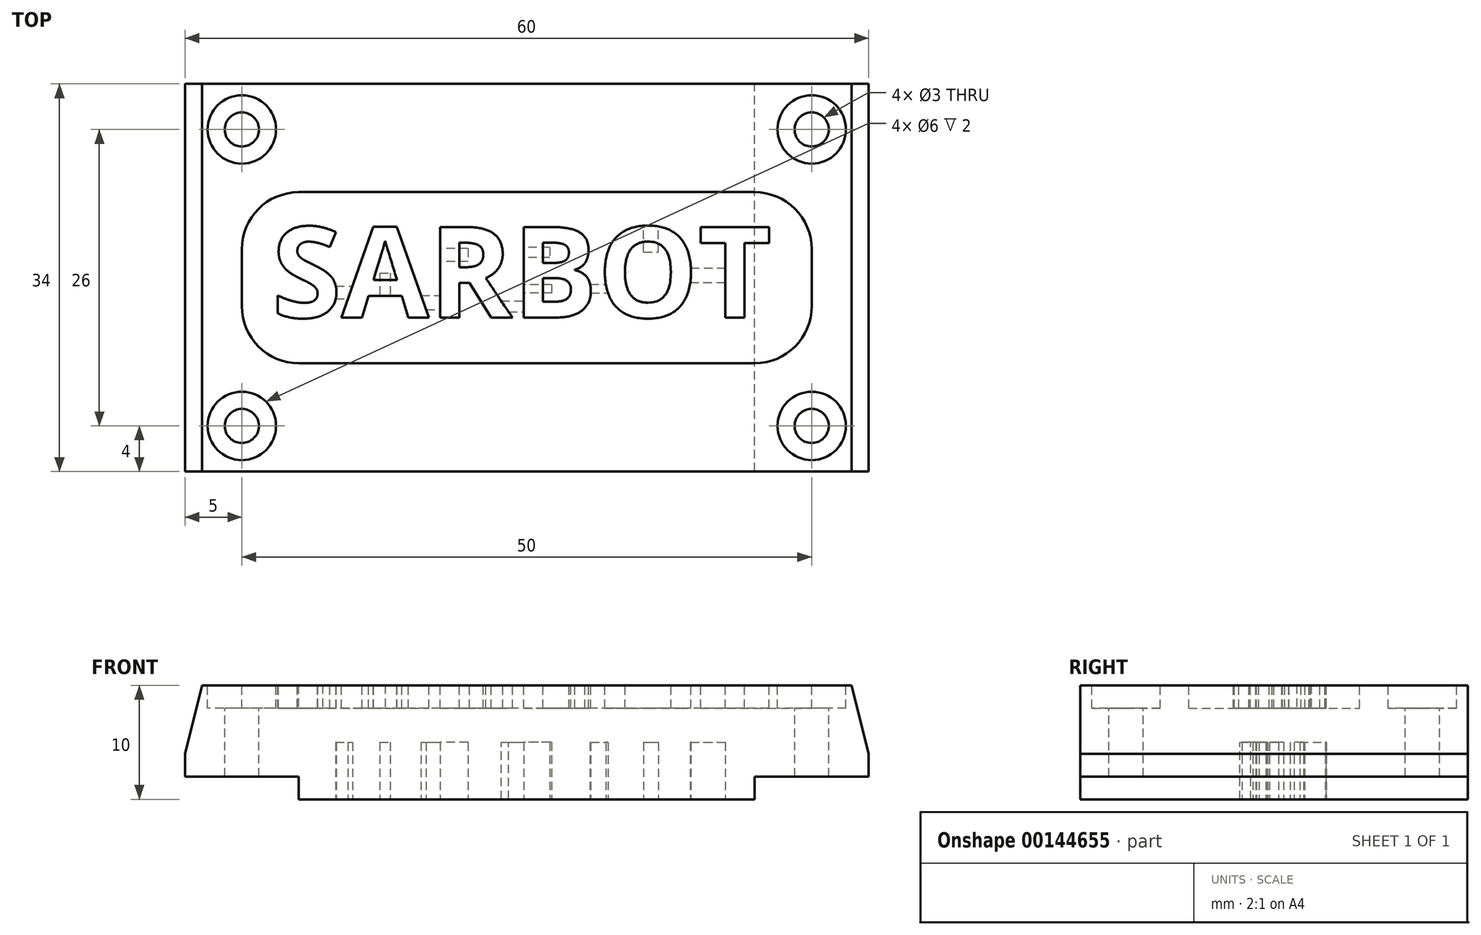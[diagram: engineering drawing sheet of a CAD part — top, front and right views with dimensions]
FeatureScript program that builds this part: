
annotation { "Feature Type Name" : "Feature", "Feature Type Description" : "" }
export const myFeature = defineFeature(function(context is Context, id is Id, definition is map)
    precondition{}
    {
        {
            var Q0;
            Q0=qCreatedBy(makeId("Top.planeOp"),FACE);
            var sketch = newSketch(context, id + "F0", { "sketchPlane" : qUnion([Q0])});
            skLineSegment(sketch, "E0.bottom", {"start": v(30, -17) * mm, "end": v(-30, -17) * mm});
            skLineSegment(sketch, "E0.top", {"start": v(30, 17) * mm, "end": v(-30, 17) * mm});
            skLineSegment(sketch, "E0.left", {"start": v(30, -17) * mm, "end": v(30, 17) * mm});
            skLineSegment(sketch, "E0.right", {"start": v(-30, -17) * mm, "end": v(-30, 17) * mm});
            skPoint(sketch, "E0.middle", {"position": v(0, 0) * mm});
            skSolve(sketch);
        }
        {
            var Q0;
            Q0=makeQuery(id+"F0.imprint","IMPRINT",FACE,{"disambiguationData":[TD([[makeQuery(id+"F0.imprint","IMPRINT",EDGE,{"derivedFrom":sQuery(id+"F0.wireOp",EDGE,"E0.bottom")}),-1.0]])]});
            extrude(context, id + "F1", {"entities" : qUnion([Q0]), "depth" : 10 * mm});
        }
        {
            var Q0;
            Q0=makeQuery(id+"F1.opExtrude","CAP_EDGE",EDGE,{"disambiguationData":[OSD([sQuery(id+"F0.wireOp",EDGE,"E0.right")])],"isStart":false});
            var Q1;
            Q1=makeQuery(id+"F1.opExtrude","CAP_EDGE",EDGE,{"disambiguationData":[OSD([sQuery(id+"F0.wireOp",EDGE,"E0.left")])],"isStart":false});
            chamfer(context, id + "F2", {"entities" : qUnion([Q0, Q1]), "chamferType" : ChamferType.TWO_OFFSETS, "width1" : 6 * mm, "oppositeDirection" : false, "width2" : 1.5 * mm, "tangentPropagation" : true});
        }
        {
            var Q0;
            Q0=makeQuery(id+"F1.opExtrude","CAP_FACE",FACE,{"disambiguationData":[OSD([sQuery(id+"F0.wireOp",EDGE,"E0.bottom"),sQuery(id+"F0.wireOp",EDGE,"E0.top"),sQuery(id+"F0.wireOp",EDGE,"E0.left"),sQuery(id+"F0.wireOp",EDGE,"E0.right")])],"isStart":true});
            var sketch = newSketch(context, id + "F3", { "sketchPlane" : qUnion([Q0])});
            skLineSegment(sketch, "E1.bottom", {"start": v(20, 17) * mm, "end": v(-20, 17) * mm});
            skLineSegment(sketch, "E1.top", {"start": v(20, -17) * mm, "end": v(-20, -17) * mm});
            skLineSegment(sketch, "E1.left", {"start": v(20, 17) * mm, "end": v(20, -17) * mm});
            skLineSegment(sketch, "E1.right", {"start": v(-20, 17) * mm, "end": v(-20, -17) * mm});
            skPoint(sketch, "E1.middle", {"position": v(0, 0) * mm});
            skSolve(sketch);
        }
        {
            var Q0;
            {var subQ0=sQuery(id+"F3.wireOp",EDGE,"E1.right");Q0=makeQuery(id+"F3.imprint","IMPRINT",FACE,{"disambiguationData":[TD([[makeQuery(id+"F3.imprint","IMPRINT",EDGE,{"derivedFrom":subQ0}),-1.0]])]});}
            var Q1;
            {var subQ0=sQuery(id+"F3.wireOp",EDGE,"E1.left");Q1=makeQuery(id+"F3.imprint","IMPRINT",FACE,{"disambiguationData":[TD([[makeQuery(id+"F3.imprint","IMPRINT",EDGE,{"derivedFrom":subQ0}),1.0]])]});}
            extrude(context, id + "F4", {"entities" : qUnion([Q0, Q1]), "operationType" : NewBodyOperationType.REMOVE, "oppositeDirection" : true, "depth" : 2 * mm});
        }
        {
            var Q0;
            Q0=makeQuery(id+"F1.opExtrude","CAP_FACE",FACE,{"disambiguationData":[OSD([sQuery(id+"F0.wireOp",EDGE,"E0.bottom"),sQuery(id+"F0.wireOp",EDGE,"E0.top"),sQuery(id+"F0.wireOp",EDGE,"E0.left"),sQuery(id+"F0.wireOp",EDGE,"E0.right")])],"isStart":false});
            var sketch = newSketch(context, id + "F5", { "sketchPlane" : qUnion([Q0])});
            skLineSegment(sketch, "E2.bottom", {"start": v(25, 13) * mm, "end": v(-25, 13) * mm});
            skLineSegment(sketch, "E2.top", {"start": v(25, -13) * mm, "end": v(-25, -13) * mm});
            skLineSegment(sketch, "E2.left", {"start": v(25, 13) * mm, "end": v(25, -13) * mm});
            skLineSegment(sketch, "E2.right", {"start": v(-25, 13) * mm, "end": v(-25, -13) * mm});
            skPoint(sketch, "E2.middle", {"position": v(0, 0) * mm});
            skText(sketch, "E3", { "text": "SARBOT", "fontName": "OpenSans-Bold.ttf"});
            skLineSegment(sketch, "E4.bottom", {"start": v(25, 7.5) * mm, "end": v(-25, 7.5) * mm});
            skLineSegment(sketch, "E4.top", {"start": v(25, -7.5) * mm, "end": v(-25, -7.5) * mm});
            skLineSegment(sketch, "E4.left", {"start": v(25, 7.5) * mm, "end": v(25, -7.5) * mm});
            skLineSegment(sketch, "E4.right", {"start": v(-25, 7.5) * mm, "end": v(-25, -7.5) * mm});
            const initialGuessF5  = {"E3": [-0.02238, -0.00349, 1, 0, 0.008]};
            skSetInitialGuess(sketch, initialGuessF5);
            skSolve(sketch);
        }
        {
            var Q0;
            Q0=sQuery(id+"F5.wireOp",VERTEX,"E2.right.start");
            var Q1;
            Q1=sQuery(id+"F5.wireOp",VERTEX,"E2.bottom.start");
            var Q2;
            Q2=sQuery(id+"F5.wireOp",VERTEX,"E2.left.end");
            var Q3;
            Q3=sQuery(id+"F5.wireOp",VERTEX,"E2.right.end");
            var Q4;
            Q4=makeQuery(id+"F1.opExtrude","SWEPT_BODY",BODY,{"disambiguationData":[OSD([sQuery(id+"F0.wireOp",EDGE,"E0.bottom"),sQuery(id+"F0.wireOp",EDGE,"E0.top"),sQuery(id+"F0.wireOp",EDGE,"E0.left"),sQuery(id+"F0.wireOp",EDGE,"E0.right")])]});
            hole(context, id + "F6", {"style" : HoleStyle.C_BORE, "endStyle" : HoleEndStyle.THROUGH, "holeDiameter" : 3 * mm, "cBoreDiameter" : 6 * mm, "cBoreDepth" : 2 * mm, "startFromSketch" : true, "locations" : qUnion([Q0, Q1, Q2, Q3]), "scope" : qUnion([Q4]), "isTappedThrough" : true});
        }
        {
            var Q0;
            Q0=makeQuery(id+"F5.imprint","IMPRINT",FACE,{"disambiguationData":[TD([[makeQuery(id+"F5.imprint","IMPRINT",EDGE,{"derivedFrom":sQuery(id+"F5.wireOp",EDGE,"E3.sketch_text.stroke-0")}),-1.0]])]});
            var Q1;
            Q1=makeQuery(id+"F5.imprint","IMPRINT",FACE,{"disambiguationData":[TD([[makeQuery(id+"F5.imprint","IMPRINT",EDGE,{"derivedFrom":sQuery(id+"F5.wireOp",EDGE,"E3.sketch_text.stroke-28")}),-1.0]])]});
            var Q2;
            Q2=makeQuery(id+"F5.imprint","IMPRINT",FACE,{"disambiguationData":[TD([[makeQuery(id+"F5.imprint","IMPRINT",EDGE,{"derivedFrom":sQuery(id+"F5.wireOp",EDGE,"E3.sketch_text.stroke-40")}),-1.0]])]});
            var Q3;
            Q3=makeQuery(id+"F5.imprint","IMPRINT",FACE,{"disambiguationData":[TD([[makeQuery(id+"F5.imprint","IMPRINT",EDGE,{"derivedFrom":sQuery(id+"F5.wireOp",EDGE,"E3.sketch_text.stroke-59")}),-1.0]])]});
            var Q4;
            Q4=makeQuery(id+"F5.imprint","IMPRINT",FACE,{"disambiguationData":[TD([[makeQuery(id+"F5.imprint","IMPRINT",EDGE,{"derivedFrom":sQuery(id+"F5.wireOp",EDGE,"E3.sketch_text.stroke-84")}),-1.0]])]});
            var Q5;
            Q5=makeQuery(id+"F5.imprint","IMPRINT",FACE,{"disambiguationData":[TD([[makeQuery(id+"F5.imprint","IMPRINT",EDGE,{"derivedFrom":sQuery(id+"F5.wireOp",EDGE,"E3.sketch_text.stroke-98")}),-1.0]])]});
            extrude(context, id + "F7", {"entities" : qUnion([Q0, Q1, Q2, Q3, Q4, Q5]), "operationType" : NewBodyOperationType.REMOVE, "oppositeDirection" : true, "depth" : 25 * mm});
        }
        {
            var Q0;
            Q0=makeQuery(id+"F5.imprint","IMPRINT",FACE,{"disambiguationData":[TD([[makeQuery(id+"F5.imprint","IMPRINT",EDGE,{"derivedFrom":sQuery(id+"F5.wireOp",EDGE,"E3.sketch_text.stroke-0")}),-1.0]])]});
            var Q1;
            Q1=makeQuery(id+"F5.imprint","IMPRINT",FACE,{"disambiguationData":[TD([[makeQuery(id+"F5.imprint","IMPRINT",EDGE,{"derivedFrom":sQuery(id+"F5.wireOp",EDGE,"E3.sketch_text.stroke-28")}),-1.0]])]});
            var Q2;
            Q2=makeQuery(id+"F5.imprint","IMPRINT",FACE,{"disambiguationData":[TD([[makeQuery(id+"F5.imprint","IMPRINT",EDGE,{"derivedFrom":sQuery(id+"F5.wireOp",EDGE,"E3.sketch_text.stroke-40")}),-1.0]])]});
            var Q3;
            Q3=makeQuery(id+"F5.imprint","IMPRINT",FACE,{"disambiguationData":[TD([[makeQuery(id+"F5.imprint","IMPRINT",EDGE,{"derivedFrom":sQuery(id+"F5.wireOp",EDGE,"E3.sketch_text.stroke-59")}),-1.0]])]});
            var Q4;
            Q4=makeQuery(id+"F5.imprint","IMPRINT",FACE,{"disambiguationData":[TD([[makeQuery(id+"F5.imprint","IMPRINT",EDGE,{"derivedFrom":sQuery(id+"F5.wireOp",EDGE,"E3.sketch_text.stroke-84")}),-1.0]])]});
            var Q5;
            Q5=makeQuery(id+"F5.imprint","IMPRINT",FACE,{"disambiguationData":[TD([[makeQuery(id+"F5.imprint","IMPRINT",EDGE,{"derivedFrom":sQuery(id+"F5.wireOp",EDGE,"E3.sketch_text.stroke-98")}),-1.0]])]});
            extrude(context, id + "F8", {"entities" : qUnion([Q0, Q1, Q2, Q3, Q4, Q5]), "oppositeDirection" : true, "depth" : 10 * mm});
        }
        {
            var Q0;
            Q0=makeQuery(id+"F5.imprint","IMPRINT",FACE,{"disambiguationData":[TD([[makeQuery(id+"F5.imprint","IMPRINT",EDGE,{"derivedFrom":sQuery(id+"F5.wireOp",EDGE,"E3.sketch_text.stroke-0")}),1.0]])]});
            var Q1;
            Q1=makeQuery(id+"F5.imprint","IMPRINT",FACE,{"disambiguationData":[TD([[makeQuery(id+"F5.imprint","IMPRINT",EDGE,{"derivedFrom":sQuery(id+"F5.wireOp",EDGE,"E3.sketch_text.stroke-36")}),1.0]])]});
            var Q2;
            Q2=makeQuery(id+"F5.imprint","IMPRINT",FACE,{"disambiguationData":[TD([[makeQuery(id+"F5.imprint","IMPRINT",EDGE,{"derivedFrom":sQuery(id+"F5.wireOp",EDGE,"E3.sketch_text.stroke-40")}),1.0]])]});
            var Q3;
            Q3=makeQuery(id+"F5.imprint","IMPRINT",FACE,{"disambiguationData":[TD([[makeQuery(id+"F5.imprint","IMPRINT",EDGE,{"derivedFrom":sQuery(id+"F5.wireOp",EDGE,"E3.sketch_text.stroke-71")}),1.0]])]});
            var Q4;
            Q4=makeQuery(id+"F5.imprint","IMPRINT",FACE,{"disambiguationData":[TD([[makeQuery(id+"F5.imprint","IMPRINT",EDGE,{"derivedFrom":sQuery(id+"F5.wireOp",EDGE,"E3.sketch_text.stroke-78")}),1.0]])]});
            var Q5;
            Q5=makeQuery(id+"F5.imprint","IMPRINT",FACE,{"disambiguationData":[TD([[makeQuery(id+"F5.imprint","IMPRINT",EDGE,{"derivedFrom":sQuery(id+"F5.wireOp",EDGE,"E3.sketch_text.stroke-92")}),1.0]])]});
            extrude(context, id + "F9", {"entities" : qUnion([Q0, Q1, Q2, Q3, Q4, Q5]), "operationType" : NewBodyOperationType.REMOVE, "oppositeDirection" : true, "depth" : 2 * mm});
        }
        {
            var Q0;
            Q0=makeQuery(id+"F9.boolean.opBoolean","COPY",EDGE,{"derivedFrom":makeQuery(id+"F9.opExtrude","SWEPT_EDGE",EDGE,{"disambiguationData":[OSD([sQuery(id+"F5.wireOp",EDGE,"E2.right"),sQuery(id+"F5.wireOp",EDGE,"E4.bottom"),sQuery(id+"F5.wireOp",EDGE,"E4.right")])]})});
            var Q1;
            Q1=makeQuery(id+"F9.boolean.opBoolean","COPY",EDGE,{"derivedFrom":makeQuery(id+"F9.opExtrude","SWEPT_EDGE",EDGE,{"disambiguationData":[OSD([sQuery(id+"F5.wireOp",EDGE,"E2.left"),sQuery(id+"F5.wireOp",EDGE,"E4.bottom"),sQuery(id+"F5.wireOp",EDGE,"E4.left")])]})});
            var Q2;
            Q2=makeQuery(id+"F9.boolean.opBoolean","COPY",EDGE,{"derivedFrom":makeQuery(id+"F9.opExtrude","SWEPT_EDGE",EDGE,{"disambiguationData":[OSD([sQuery(id+"F5.wireOp",EDGE,"E2.right"),sQuery(id+"F5.wireOp",EDGE,"E4.top"),sQuery(id+"F5.wireOp",EDGE,"E4.right")])]})});
            var Q3;
            Q3=makeQuery(id+"F9.boolean.opBoolean","COPY",EDGE,{"derivedFrom":makeQuery(id+"F9.opExtrude","SWEPT_EDGE",EDGE,{"disambiguationData":[OSD([sQuery(id+"F5.wireOp",EDGE,"E2.left"),sQuery(id+"F5.wireOp",EDGE,"E4.top"),sQuery(id+"F5.wireOp",EDGE,"E4.left")])]})});
            fillet(context, id + "F10", {"entities" : qUnion([Q0, Q1, Q2, Q3]), "radius" : 5 * mm, "tangentPropagation" : true, "allowEdgeOverflow" : false});
        }
        {
            var Q0;
            {var subQ0=sQuery(id+"F0.wireOp",EDGE,"E0.bottom");var subQ1=sQuery(id+"F0.wireOp",EDGE,"E0.top");Q0=makeQuery(id+"F7.boolean.opBoolean","SPLIT",FACE,{"disambiguationData":[TD([makeQuery(id+"F1.opExtrude","SWEPT_FACE",FACE,{"disambiguationData":[OSD([subQ0])]})])],"derivedFrom":makeQuery(id+"F1.opExtrude","CAP_FACE",FACE,{"disambiguationData":[OSD([subQ0,subQ1,sQuery(id+"F0.wireOp",EDGE,"E0.left"),sQuery(id+"F0.wireOp",EDGE,"E0.right")])],"isStart":true})});}
            var sketch = newSketch(context, id + "F11", { "sketchPlane" : qUnion([Q0])});
            skLineSegment(sketch, "E5.bottom", {"start": v(-12.9, -0.4) * mm, "end": v(-11.99, -0.4) * mm});
            skLineSegment(sketch, "E5.top", {"start": v(-12.9, 2.92) * mm, "end": v(-11.99, 2.92) * mm});
            skLineSegment(sketch, "E5.left", {"start": v(-12.9, -0.4) * mm, "end": v(-12.9, 2.92) * mm});
            skLineSegment(sketch, "E5.right", {"start": v(-11.99, -0.4) * mm, "end": v(-11.99, 2.92) * mm});
            skLineSegment(sketch, "E6.bottom", {"start": v(-5.16, -2.56) * mm, "end": v(-8.52, -2.56) * mm});
            skLineSegment(sketch, "E6.top", {"start": v(-5.16, -1.41) * mm, "end": v(-8.52, -1.41) * mm});
            skLineSegment(sketch, "E6.left", {"start": v(-5.16, -2.56) * mm, "end": v(-5.16, -1.41) * mm});
            skLineSegment(sketch, "E6.right", {"start": v(-8.52, -2.56) * mm, "end": v(-8.52, -1.41) * mm});
            skLineSegment(sketch, "E7.bottom", {"start": v(2.03, -2.67) * mm, "end": v(-1.26, -2.67) * mm});
            skLineSegment(sketch, "E7.top", {"start": v(2.03, -1.76) * mm, "end": v(-1.26, -1.76) * mm});
            skLineSegment(sketch, "E7.left", {"start": v(2.03, -2.67) * mm, "end": v(2.03, -1.76) * mm});
            skLineSegment(sketch, "E7.right", {"start": v(-1.26, -2.67) * mm, "end": v(-1.26, -1.76) * mm});
            skLineSegment(sketch, "E8.bottom", {"start": v(2.18, 0.6) * mm, "end": v(-1.22, 0.6) * mm});
            skLineSegment(sketch, "E8.top", {"start": v(2.18, 1.34) * mm, "end": v(-1.22, 1.34) * mm});
            skLineSegment(sketch, "E8.left", {"start": v(2.18, 0.6) * mm, "end": v(2.18, 1.34) * mm});
            skLineSegment(sketch, "E8.right", {"start": v(-1.22, 0.6) * mm, "end": v(-1.22, 1.34) * mm});
            skLineSegment(sketch, "E9.bottom", {"start": v(10.24, -2.24) * mm, "end": v(11.56, -2.24) * mm});
            skLineSegment(sketch, "E9.top", {"start": v(10.24, -5.78) * mm, "end": v(11.56, -5.78) * mm});
            skLineSegment(sketch, "E9.left", {"start": v(10.24, -2.24) * mm, "end": v(10.24, -5.78) * mm});
            skLineSegment(sketch, "E9.right", {"start": v(11.56, -2.24) * mm, "end": v(11.56, -5.78) * mm});
            skLineSegment(sketch, "E10.bottom", {"start": v(-17.47, 1.86) * mm, "end": v(-14.77, 1.86) * mm});
            skLineSegment(sketch, "E10.top", {"start": v(-17.47, 0.73) * mm, "end": v(-14.77, 0.73) * mm});
            skLineSegment(sketch, "E10.left", {"start": v(-17.47, 1.86) * mm, "end": v(-17.47, 0.73) * mm});
            skLineSegment(sketch, "E10.right", {"start": v(-14.77, 1.86) * mm, "end": v(-14.77, 0.73) * mm});
            skLineSegment(sketch, "E11.bottom", {"start": v(-9.8, 2.81) * mm, "end": v(-6.93, 2.81) * mm});
            skLineSegment(sketch, "E11.top", {"start": v(-9.8, 1.56) * mm, "end": v(-6.93, 1.56) * mm});
            skLineSegment(sketch, "E11.left", {"start": v(-9.8, 2.81) * mm, "end": v(-9.8, 1.56) * mm});
            skLineSegment(sketch, "E11.right", {"start": v(-6.93, 2.81) * mm, "end": v(-6.93, 1.56) * mm});
            skLineSegment(sketch, "E12.bottom", {"start": v(-2.64, 3) * mm, "end": v(0.52, 3) * mm});
            skLineSegment(sketch, "E12.top", {"start": v(-2.64, 2.05) * mm, "end": v(0.52, 2.05) * mm});
            skLineSegment(sketch, "E12.left", {"start": v(-2.64, 3) * mm, "end": v(-2.64, 2.05) * mm});
            skLineSegment(sketch, "E12.right", {"start": v(0.52, 3) * mm, "end": v(0.52, 2.05) * mm});
            skLineSegment(sketch, "E13.bottom", {"start": v(4.78, 1.34) * mm, "end": v(7.72, 1.34) * mm});
            skLineSegment(sketch, "E13.top", {"start": v(4.78, 0.58) * mm, "end": v(7.72, 0.58) * mm});
            skLineSegment(sketch, "E13.left", {"start": v(4.78, 1.34) * mm, "end": v(4.78, 0.58) * mm});
            skLineSegment(sketch, "E13.right", {"start": v(7.72, 1.34) * mm, "end": v(7.72, 0.58) * mm});
            skLineSegment(sketch, "E14.bottom", {"start": v(13.43, 0.42) * mm, "end": v(18.24, 0.42) * mm});
            skLineSegment(sketch, "E14.top", {"start": v(13.43, -0.84) * mm, "end": v(18.24, -0.84) * mm});
            skLineSegment(sketch, "E14.left", {"start": v(13.43, 0.42) * mm, "end": v(13.43, -0.84) * mm});
            skLineSegment(sketch, "E14.right", {"start": v(18.24, 0.42) * mm, "end": v(18.24, -0.84) * mm});
            skSolve(sketch);
        }
        {
            var Q0;
            {var subQ0=sQuery(id+"F11.wireOp",EDGE,"E5.top");Q0=makeQuery(id+"F11.imprint","IMPRINT",FACE,{"disambiguationData":[TD([[makeQuery(id+"F11.imprint","IMPRINT",EDGE,{"derivedFrom":subQ0}),-1.0]])]});}
            var Q1;
            {var subQ0=sQuery(id+"F11.wireOp",EDGE,"E5.bottom");Q1=makeQuery(id+"F11.imprint","IMPRINT",FACE,{"disambiguationData":[TD([[makeQuery(id+"F11.imprint","IMPRINT",EDGE,{"derivedFrom":subQ0}),1.0]])]});}
            var Q2;
            {var subQ0=sQuery(id+"F11.wireOp",EDGE,"E6.right");Q2=makeQuery(id+"F11.imprint","IMPRINT",FACE,{"disambiguationData":[TD([[makeQuery(id+"F11.imprint","IMPRINT",EDGE,{"derivedFrom":subQ0}),-1.0]])]});}
            var Q3;
            {var subQ0=sQuery(id+"F11.wireOp",EDGE,"E6.left");Q3=makeQuery(id+"F11.imprint","IMPRINT",FACE,{"disambiguationData":[TD([[makeQuery(id+"F11.imprint","IMPRINT",EDGE,{"derivedFrom":subQ0}),1.0]])]});}
            var Q4;
            {var subQ0=sQuery(id+"F11.wireOp",EDGE,"E7.left");Q4=makeQuery(id+"F11.imprint","IMPRINT",FACE,{"disambiguationData":[TD([[makeQuery(id+"F11.imprint","IMPRINT",EDGE,{"derivedFrom":subQ0}),1.0]])]});}
            var Q5;
            {var subQ0=sQuery(id+"F11.wireOp",EDGE,"E7.right");Q5=makeQuery(id+"F11.imprint","IMPRINT",FACE,{"disambiguationData":[TD([[makeQuery(id+"F11.imprint","IMPRINT",EDGE,{"derivedFrom":subQ0}),-1.0]])]});}
            var Q6;
            {var subQ0=sQuery(id+"F11.wireOp",EDGE,"E8.right");Q6=makeQuery(id+"F11.imprint","IMPRINT",FACE,{"disambiguationData":[TD([[makeQuery(id+"F11.imprint","IMPRINT",EDGE,{"derivedFrom":subQ0}),-1.0]])]});}
            var Q7;
            {var subQ0=sQuery(id+"F11.wireOp",EDGE,"E8.left");Q7=makeQuery(id+"F11.imprint","IMPRINT",FACE,{"disambiguationData":[TD([[makeQuery(id+"F11.imprint","IMPRINT",EDGE,{"derivedFrom":subQ0}),1.0]])]});}
            var Q8;
            {var subQ7=sQuery(id+"F11.wireOp",EDGE,"E9.top");Q8=makeQuery(id+"F11.imprint","IMPRINT",FACE,{"disambiguationData":[TD([[makeQuery(id+"F11.imprint","IMPRINT",EDGE,{"derivedFrom":subQ7}),1.0]])]});}
            var Q9;
            {var subQ8=sQuery(id+"F11.wireOp",EDGE,"E9.bottom");Q9=makeQuery(id+"F11.imprint","IMPRINT",FACE,{"disambiguationData":[TD([[makeQuery(id+"F11.imprint","IMPRINT",EDGE,{"derivedFrom":subQ8}),-1.0]])]});}
            extrude(context, id + "F12", {"entities" : qUnion([Q0, Q1, Q2, Q3, Q4, Q5, Q6, Q7, Q8, Q9]), "operationType" : NewBodyOperationType.ADD, "oppositeDirection" : true, "depth" : 5 * mm});
        }
        {
            var Q0;
            {var subQ0=sQuery(id+"F11.wireOp",EDGE,"E5.bottom");Q0=makeQuery(id+"F11.imprint","IMPRINT",FACE,{"disambiguationData":[TD([[makeQuery(id+"F11.imprint","IMPRINT",EDGE,{"derivedFrom":subQ0}),1.0]])]});}
            var Q1;
            {var subQ0=sQuery(id+"F11.wireOp",EDGE,"E6.left");Q1=makeQuery(id+"F11.imprint","IMPRINT",FACE,{"disambiguationData":[TD([[makeQuery(id+"F11.imprint","IMPRINT",EDGE,{"derivedFrom":subQ0}),1.0]])]});}
            var Q2;
            {var subQ0=sQuery(id+"F11.wireOp",EDGE,"E7.left");Q2=makeQuery(id+"F11.imprint","IMPRINT",FACE,{"disambiguationData":[TD([[makeQuery(id+"F11.imprint","IMPRINT",EDGE,{"derivedFrom":subQ0}),1.0]])]});}
            var Q3;
            {var subQ0=sQuery(id+"F11.wireOp",EDGE,"E8.left");Q3=makeQuery(id+"F11.imprint","IMPRINT",FACE,{"disambiguationData":[TD([[makeQuery(id+"F11.imprint","IMPRINT",EDGE,{"derivedFrom":subQ0}),1.0]])]});}
            var Q4;
            {var subQ8=sQuery(id+"F11.wireOp",EDGE,"E9.bottom");Q4=makeQuery(id+"F11.imprint","IMPRINT",FACE,{"disambiguationData":[TD([[makeQuery(id+"F11.imprint","IMPRINT",EDGE,{"derivedFrom":subQ8}),-1.0]])]});}
            extrude(context, id + "F13", {"entities" : qUnion([Q0, Q1, Q2, Q3, Q4]), "operationType" : NewBodyOperationType.REMOVE, "oppositeDirection" : true, "depth" : 5 * mm});
        }
        {
            var Q0;
            {var subQ6=sQuery(id+"F11.wireOp",EDGE,"E10.left");Q0=makeQuery(id+"F11.imprint","IMPRINT",FACE,{"disambiguationData":[TD([[makeQuery(id+"F11.imprint","IMPRINT",EDGE,{"derivedFrom":subQ6}),1.0]])]});}
            var Q1;
            {var subQ0=makeQuery(id+"F1.opExtrude","CAP_FACE",FACE,{"disambiguationData":[OSD([sQuery(id+"F0.wireOp",EDGE,"E0.bottom"),sQuery(id+"F0.wireOp",EDGE,"E0.top"),sQuery(id+"F0.wireOp",EDGE,"E0.left"),sQuery(id+"F0.wireOp",EDGE,"E0.right")])],"isStart":true});var subQ2=makeQuery(id+"F7.boolean.opBoolean","INTERSECT",EDGE,{"derivedFrom":[subQ0,makeQuery(id+"F7.opExtrude","SWEPT_FACE",FACE,{"disambiguationData":[OSD([sQuery(id+"F5.wireOp",EDGE,"E3.sketch_text.stroke-0")])]})]});var subQ8=sQuery(id+"F11.wireOp",EDGE,"E10.bottom");var subQ9=makeQuery(id+"F11.imprint","INTERSECT",VERTEX,{"derivedFrom":[subQ2,subQ8]});Q1=makeQuery(id+"F11.imprint","IMPRINT",FACE,{"disambiguationData":[TD([[makeQuery(id+"F11.imprint","IMPRINT",EDGE,{"disambiguationData":[TD([[subQ9,-1.0]])],"derivedFrom":subQ8}),-1.0]])]});}
            var Q2;
            {var subQ0=sQuery(id+"F11.wireOp",EDGE,"E10.right");Q2=makeQuery(id+"F11.imprint","IMPRINT",FACE,{"disambiguationData":[TD([[makeQuery(id+"F11.imprint","IMPRINT",EDGE,{"derivedFrom":subQ0}),-1.0]])]});}
            var Q3;
            {var subQ0=sQuery(id+"F11.wireOp",EDGE,"E11.left");Q3=makeQuery(id+"F11.imprint","IMPRINT",FACE,{"disambiguationData":[TD([[makeQuery(id+"F11.imprint","IMPRINT",EDGE,{"derivedFrom":subQ0}),1.0]])]});}
            var Q4;
            {var subQ0=sQuery(id+"F11.wireOp",EDGE,"E11.bottom");var subQ1=makeQuery(id+"F1.opExtrude","CAP_FACE",FACE,{"disambiguationData":[OSD([sQuery(id+"F0.wireOp",EDGE,"E0.bottom"),sQuery(id+"F0.wireOp",EDGE,"E0.top"),sQuery(id+"F0.wireOp",EDGE,"E0.left"),sQuery(id+"F0.wireOp",EDGE,"E0.right")])],"isStart":true});var subQ2=makeQuery(id+"F7.boolean.opBoolean","INTERSECT",EDGE,{"derivedFrom":[subQ1,makeQuery(id+"F7.opExtrude","SWEPT_FACE",FACE,{"disambiguationData":[OSD([sQuery(id+"F5.wireOp",EDGE,"E3.sketch_text.stroke-34")])]})]});var subQ3=makeQuery(id+"F11.imprint","INTERSECT",VERTEX,{"derivedFrom":[subQ2,subQ0]});Q4=makeQuery(id+"F11.imprint","IMPRINT",FACE,{"disambiguationData":[TD([[makeQuery(id+"F11.imprint","IMPRINT",EDGE,{"disambiguationData":[TD([[subQ3,-1.0]])],"derivedFrom":subQ0}),-1.0]])]});}
            var Q5;
            {var subQ0=sQuery(id+"F11.wireOp",EDGE,"E11.right");Q5=makeQuery(id+"F11.imprint","IMPRINT",FACE,{"disambiguationData":[TD([[makeQuery(id+"F11.imprint","IMPRINT",EDGE,{"derivedFrom":subQ0}),-1.0]])]});}
            var Q6;
            {var subQ0=sQuery(id+"F11.wireOp",EDGE,"E12.left");Q6=makeQuery(id+"F11.imprint","IMPRINT",FACE,{"disambiguationData":[TD([[makeQuery(id+"F11.imprint","IMPRINT",EDGE,{"derivedFrom":subQ0}),1.0]])]});}
            var Q7;
            {var subQ0=sQuery(id+"F11.wireOp",EDGE,"E12.bottom");var subQ1=makeQuery(id+"F1.opExtrude","CAP_FACE",FACE,{"disambiguationData":[OSD([sQuery(id+"F0.wireOp",EDGE,"E0.bottom"),sQuery(id+"F0.wireOp",EDGE,"E0.top"),sQuery(id+"F0.wireOp",EDGE,"E0.left"),sQuery(id+"F0.wireOp",EDGE,"E0.right")])],"isStart":true});var subQ2=makeQuery(id+"F7.boolean.opBoolean","INTERSECT",EDGE,{"derivedFrom":[subQ1,makeQuery(id+"F7.opExtrude","SWEPT_FACE",FACE,{"disambiguationData":[OSD([sQuery(id+"F5.wireOp",EDGE,"E3.sketch_text.stroke-55")])]})]});var subQ3=makeQuery(id+"F11.imprint","INTERSECT",VERTEX,{"derivedFrom":[subQ2,subQ0]});Q7=makeQuery(id+"F11.imprint","IMPRINT",FACE,{"disambiguationData":[TD([[makeQuery(id+"F11.imprint","IMPRINT",EDGE,{"disambiguationData":[TD([[subQ3,-1.0]])],"derivedFrom":subQ0}),-1.0]])]});}
            var Q8;
            {var subQ0=sQuery(id+"F11.wireOp",EDGE,"E12.right");Q8=makeQuery(id+"F11.imprint","IMPRINT",FACE,{"disambiguationData":[TD([[makeQuery(id+"F11.imprint","IMPRINT",EDGE,{"derivedFrom":subQ0}),-1.0]])]});}
            var Q9;
            {var subQ6=sQuery(id+"F11.wireOp",EDGE,"E13.left");Q9=makeQuery(id+"F11.imprint","IMPRINT",FACE,{"disambiguationData":[TD([[makeQuery(id+"F11.imprint","IMPRINT",EDGE,{"derivedFrom":subQ6}),1.0]])]});}
            var Q10;
            {var subQ0=makeQuery(id+"F1.opExtrude","CAP_FACE",FACE,{"disambiguationData":[OSD([sQuery(id+"F0.wireOp",EDGE,"E0.bottom"),sQuery(id+"F0.wireOp",EDGE,"E0.top"),sQuery(id+"F0.wireOp",EDGE,"E0.left"),sQuery(id+"F0.wireOp",EDGE,"E0.right")])],"isStart":true});var subQ1=makeQuery(id+"F7.boolean.opBoolean","INTERSECT",EDGE,{"derivedFrom":[subQ0,makeQuery(id+"F7.opExtrude","SWEPT_FACE",FACE,{"disambiguationData":[OSD([sQuery(id+"F5.wireOp",EDGE,"E3.sketch_text.stroke-67")])]})]});var subQ4=sQuery(id+"F11.wireOp",EDGE,"E13.bottom");var subQ5=makeQuery(id+"F11.imprint","INTERSECT",VERTEX,{"derivedFrom":[subQ1,subQ4]});Q10=makeQuery(id+"F11.imprint","IMPRINT",FACE,{"disambiguationData":[TD([[makeQuery(id+"F11.imprint","IMPRINT",EDGE,{"disambiguationData":[TD([[subQ5,-1.0]])],"derivedFrom":subQ4}),-1.0]])]});}
            var Q11;
            {var subQ0=sQuery(id+"F11.wireOp",EDGE,"E13.right");Q11=makeQuery(id+"F11.imprint","IMPRINT",FACE,{"disambiguationData":[TD([[makeQuery(id+"F11.imprint","IMPRINT",EDGE,{"derivedFrom":subQ0}),-1.0]])]});}
            var Q12;
            {var subQ6=sQuery(id+"F11.wireOp",EDGE,"E14.left");Q12=makeQuery(id+"F11.imprint","IMPRINT",FACE,{"disambiguationData":[TD([[makeQuery(id+"F11.imprint","IMPRINT",EDGE,{"derivedFrom":subQ6}),1.0]])]});}
            var Q13;
            {var subQ0=makeQuery(id+"F1.opExtrude","CAP_FACE",FACE,{"disambiguationData":[OSD([sQuery(id+"F0.wireOp",EDGE,"E0.bottom"),sQuery(id+"F0.wireOp",EDGE,"E0.top"),sQuery(id+"F0.wireOp",EDGE,"E0.left"),sQuery(id+"F0.wireOp",EDGE,"E0.right")])],"isStart":true});var subQ4=sQuery(id+"F11.wireOp",EDGE,"E14.bottom");var subQ7=makeQuery(id+"F7.boolean.opBoolean","INTERSECT",EDGE,{"derivedFrom":[subQ0,makeQuery(id+"F7.opExtrude","SWEPT_FACE",FACE,{"disambiguationData":[OSD([sQuery(id+"F5.wireOp",EDGE,"E3.sketch_text.stroke-99")])]})]});var subQ10=makeQuery(id+"F11.imprint","INTERSECT",VERTEX,{"derivedFrom":[subQ7,subQ4]});Q13=makeQuery(id+"F11.imprint","IMPRINT",FACE,{"disambiguationData":[TD([[makeQuery(id+"F11.imprint","IMPRINT",EDGE,{"disambiguationData":[TD([[subQ10,1.0]])],"derivedFrom":subQ4}),-1.0]])]});}
            var Q14;
            {var subQ0=sQuery(id+"F11.wireOp",EDGE,"E14.right");Q14=makeQuery(id+"F11.imprint","IMPRINT",FACE,{"disambiguationData":[TD([[makeQuery(id+"F11.imprint","IMPRINT",EDGE,{"derivedFrom":subQ0}),-1.0]])]});}
            extrude(context, id + "F14", {"entities" : qUnion([Q0, Q1, Q2, Q3, Q4, Q5, Q6, Q7, Q8, Q9, Q10, Q11, Q12, Q13, Q14]), "operationType" : NewBodyOperationType.ADD, "oppositeDirection" : true, "depth" : 5 * mm});
        }
        {
            var Q0;
            {var subQ0=makeQuery(id+"F1.opExtrude","CAP_FACE",FACE,{"disambiguationData":[OSD([sQuery(id+"F0.wireOp",EDGE,"E0.bottom"),sQuery(id+"F0.wireOp",EDGE,"E0.top"),sQuery(id+"F0.wireOp",EDGE,"E0.left"),sQuery(id+"F0.wireOp",EDGE,"E0.right")])],"isStart":true});var subQ2=makeQuery(id+"F7.boolean.opBoolean","INTERSECT",EDGE,{"derivedFrom":[subQ0,makeQuery(id+"F7.opExtrude","SWEPT_FACE",FACE,{"disambiguationData":[OSD([sQuery(id+"F5.wireOp",EDGE,"E3.sketch_text.stroke-0")])]})]});var subQ8=sQuery(id+"F11.wireOp",EDGE,"E10.bottom");var subQ9=makeQuery(id+"F11.imprint","INTERSECT",VERTEX,{"derivedFrom":[subQ2,subQ8]});Q0=makeQuery(id+"F11.imprint","IMPRINT",FACE,{"disambiguationData":[TD([[makeQuery(id+"F11.imprint","IMPRINT",EDGE,{"disambiguationData":[TD([[subQ9,-1.0]])],"derivedFrom":subQ8}),-1.0]])]});}
            var Q1;
            {var subQ0=sQuery(id+"F11.wireOp",EDGE,"E11.bottom");var subQ1=makeQuery(id+"F1.opExtrude","CAP_FACE",FACE,{"disambiguationData":[OSD([sQuery(id+"F0.wireOp",EDGE,"E0.bottom"),sQuery(id+"F0.wireOp",EDGE,"E0.top"),sQuery(id+"F0.wireOp",EDGE,"E0.left"),sQuery(id+"F0.wireOp",EDGE,"E0.right")])],"isStart":true});var subQ2=makeQuery(id+"F7.boolean.opBoolean","INTERSECT",EDGE,{"derivedFrom":[subQ1,makeQuery(id+"F7.opExtrude","SWEPT_FACE",FACE,{"disambiguationData":[OSD([sQuery(id+"F5.wireOp",EDGE,"E3.sketch_text.stroke-34")])]})]});var subQ3=makeQuery(id+"F11.imprint","INTERSECT",VERTEX,{"derivedFrom":[subQ2,subQ0]});Q1=makeQuery(id+"F11.imprint","IMPRINT",FACE,{"disambiguationData":[TD([[makeQuery(id+"F11.imprint","IMPRINT",EDGE,{"disambiguationData":[TD([[subQ3,-1.0]])],"derivedFrom":subQ0}),-1.0]])]});}
            var Q2;
            {var subQ0=sQuery(id+"F11.wireOp",EDGE,"E12.bottom");var subQ1=makeQuery(id+"F1.opExtrude","CAP_FACE",FACE,{"disambiguationData":[OSD([sQuery(id+"F0.wireOp",EDGE,"E0.bottom"),sQuery(id+"F0.wireOp",EDGE,"E0.top"),sQuery(id+"F0.wireOp",EDGE,"E0.left"),sQuery(id+"F0.wireOp",EDGE,"E0.right")])],"isStart":true});var subQ2=makeQuery(id+"F7.boolean.opBoolean","INTERSECT",EDGE,{"derivedFrom":[subQ1,makeQuery(id+"F7.opExtrude","SWEPT_FACE",FACE,{"disambiguationData":[OSD([sQuery(id+"F5.wireOp",EDGE,"E3.sketch_text.stroke-55")])]})]});var subQ3=makeQuery(id+"F11.imprint","INTERSECT",VERTEX,{"derivedFrom":[subQ2,subQ0]});Q2=makeQuery(id+"F11.imprint","IMPRINT",FACE,{"disambiguationData":[TD([[makeQuery(id+"F11.imprint","IMPRINT",EDGE,{"disambiguationData":[TD([[subQ3,-1.0]])],"derivedFrom":subQ0}),-1.0]])]});}
            var Q3;
            {var subQ0=makeQuery(id+"F1.opExtrude","CAP_FACE",FACE,{"disambiguationData":[OSD([sQuery(id+"F0.wireOp",EDGE,"E0.bottom"),sQuery(id+"F0.wireOp",EDGE,"E0.top"),sQuery(id+"F0.wireOp",EDGE,"E0.left"),sQuery(id+"F0.wireOp",EDGE,"E0.right")])],"isStart":true});var subQ1=makeQuery(id+"F7.boolean.opBoolean","INTERSECT",EDGE,{"derivedFrom":[subQ0,makeQuery(id+"F7.opExtrude","SWEPT_FACE",FACE,{"disambiguationData":[OSD([sQuery(id+"F5.wireOp",EDGE,"E3.sketch_text.stroke-67")])]})]});var subQ4=sQuery(id+"F11.wireOp",EDGE,"E13.bottom");var subQ5=makeQuery(id+"F11.imprint","INTERSECT",VERTEX,{"derivedFrom":[subQ1,subQ4]});Q3=makeQuery(id+"F11.imprint","IMPRINT",FACE,{"disambiguationData":[TD([[makeQuery(id+"F11.imprint","IMPRINT",EDGE,{"disambiguationData":[TD([[subQ5,-1.0]])],"derivedFrom":subQ4}),-1.0]])]});}
            var Q4;
            {var subQ0=makeQuery(id+"F1.opExtrude","CAP_FACE",FACE,{"disambiguationData":[OSD([sQuery(id+"F0.wireOp",EDGE,"E0.bottom"),sQuery(id+"F0.wireOp",EDGE,"E0.top"),sQuery(id+"F0.wireOp",EDGE,"E0.left"),sQuery(id+"F0.wireOp",EDGE,"E0.right")])],"isStart":true});var subQ4=sQuery(id+"F11.wireOp",EDGE,"E14.bottom");var subQ7=makeQuery(id+"F7.boolean.opBoolean","INTERSECT",EDGE,{"derivedFrom":[subQ0,makeQuery(id+"F7.opExtrude","SWEPT_FACE",FACE,{"disambiguationData":[OSD([sQuery(id+"F5.wireOp",EDGE,"E3.sketch_text.stroke-99")])]})]});var subQ10=makeQuery(id+"F11.imprint","INTERSECT",VERTEX,{"derivedFrom":[subQ7,subQ4]});Q4=makeQuery(id+"F11.imprint","IMPRINT",FACE,{"disambiguationData":[TD([[makeQuery(id+"F11.imprint","IMPRINT",EDGE,{"disambiguationData":[TD([[subQ10,1.0]])],"derivedFrom":subQ4}),-1.0]])]});}
            extrude(context, id + "F15", {"entities" : qUnion([Q0, Q1, Q2, Q3, Q4]), "operationType" : NewBodyOperationType.REMOVE, "oppositeDirection" : true, "depth" : 5 * mm});
        }
        {
            var Q0;
            Q0=makeQuery(id+"F14.boolean.opBoolean","MERGE",FACE,{"derivedFrom":[makeQuery(id+"F8.opExtrude","CAP_FACE",FACE,{"disambiguationData":[OSD([sQuery(id+"F5.wireOp",EDGE,"E3.sketch_text.stroke-0"),sQuery(id+"F5.wireOp",EDGE,"E3.sketch_text.stroke-1"),sQuery(id+"F5.wireOp",EDGE,"E3.sketch_text.stroke-2"),sQuery(id+"F5.wireOp",EDGE,"E3.sketch_text.stroke-3"),sQuery(id+"F5.wireOp",EDGE,"E3.sketch_text.stroke-4"),sQuery(id+"F5.wireOp",EDGE,"E3.sketch_text.stroke-5"),sQuery(id+"F5.wireOp",EDGE,"E3.sketch_text.stroke-6"),sQuery(id+"F5.wireOp",EDGE,"E3.sketch_text.stroke-7"),sQuery(id+"F5.wireOp",EDGE,"E3.sketch_text.stroke-8"),sQuery(id+"F5.wireOp",EDGE,"E3.sketch_text.stroke-9"),sQuery(id+"F5.wireOp",EDGE,"E3.sketch_text.stroke-10"),sQuery(id+"F5.wireOp",EDGE,"E3.sketch_text.stroke-11"),sQuery(id+"F5.wireOp",EDGE,"E3.sketch_text.stroke-12"),sQuery(id+"F5.wireOp",EDGE,"E3.sketch_text.stroke-13"),sQuery(id+"F5.wireOp",EDGE,"E3.sketch_text.stroke-14"),sQuery(id+"F5.wireOp",EDGE,"E3.sketch_text.stroke-15"),sQuery(id+"F5.wireOp",EDGE,"E3.sketch_text.stroke-16"),sQuery(id+"F5.wireOp",EDGE,"E3.sketch_text.stroke-17"),sQuery(id+"F5.wireOp",EDGE,"E3.sketch_text.stroke-18"),sQuery(id+"F5.wireOp",EDGE,"E3.sketch_text.stroke-19"),sQuery(id+"F5.wireOp",EDGE,"E3.sketch_text.stroke-20"),sQuery(id+"F5.wireOp",EDGE,"E3.sketch_text.stroke-21"),sQuery(id+"F5.wireOp",EDGE,"E3.sketch_text.stroke-22"),sQuery(id+"F5.wireOp",EDGE,"E3.sketch_text.stroke-23"),sQuery(id+"F5.wireOp",EDGE,"E3.sketch_text.stroke-24"),sQuery(id+"F5.wireOp",EDGE,"E3.sketch_text.stroke-25"),sQuery(id+"F5.wireOp",EDGE,"E3.sketch_text.stroke-26"),sQuery(id+"F5.wireOp",EDGE,"E3.sketch_text.stroke-27")])],"isStart":false}),makeQuery(id+"F8.opExtrude","CAP_FACE",FACE,{"disambiguationData":[OSD([sQuery(id+"F5.wireOp",EDGE,"E3.sketch_text.stroke-98"),sQuery(id+"F5.wireOp",EDGE,"E3.sketch_text.stroke-99"),sQuery(id+"F5.wireOp",EDGE,"E3.sketch_text.stroke-100"),sQuery(id+"F5.wireOp",EDGE,"E3.sketch_text.stroke-101"),sQuery(id+"F5.wireOp",EDGE,"E3.sketch_text.stroke-102"),sQuery(id+"F5.wireOp",EDGE,"E3.sketch_text.stroke-103"),sQuery(id+"F5.wireOp",EDGE,"E3.sketch_text.stroke-104"),sQuery(id+"F5.wireOp",EDGE,"E3.sketch_text.stroke-105")])],"isStart":false}),makeQuery(id+"F8.opExtrude","CAP_FACE",FACE,{"disambiguationData":[OSD([sQuery(id+"F5.wireOp",EDGE,"E3.sketch_text.stroke-28"),sQuery(id+"F5.wireOp",EDGE,"E3.sketch_text.stroke-29"),sQuery(id+"F5.wireOp",EDGE,"E3.sketch_text.stroke-30"),sQuery(id+"F5.wireOp",EDGE,"E3.sketch_text.stroke-31"),sQuery(id+"F5.wireOp",EDGE,"E3.sketch_text.stroke-32"),sQuery(id+"F5.wireOp",EDGE,"E3.sketch_text.stroke-33"),sQuery(id+"F5.wireOp",EDGE,"E3.sketch_text.stroke-34"),sQuery(id+"F5.wireOp",EDGE,"E3.sketch_text.stroke-35"),sQuery(id+"F5.wireOp",EDGE,"E3.sketch_text.stroke-36"),sQuery(id+"F5.wireOp",EDGE,"E3.sketch_text.stroke-37"),sQuery(id+"F5.wireOp",EDGE,"E3.sketch_text.stroke-38"),sQuery(id+"F5.wireOp",EDGE,"E3.sketch_text.stroke-39")])],"isStart":false}),makeQuery(id+"F8.opExtrude","CAP_FACE",FACE,{"disambiguationData":[OSD([sQuery(id+"F5.wireOp",EDGE,"E3.sketch_text.stroke-40"),sQuery(id+"F5.wireOp",EDGE,"E3.sketch_text.stroke-41"),sQuery(id+"F5.wireOp",EDGE,"E3.sketch_text.stroke-42"),sQuery(id+"F5.wireOp",EDGE,"E3.sketch_text.stroke-43"),sQuery(id+"F5.wireOp",EDGE,"E3.sketch_text.stroke-44"),sQuery(id+"F5.wireOp",EDGE,"E3.sketch_text.stroke-45"),sQuery(id+"F5.wireOp",EDGE,"E3.sketch_text.stroke-46"),sQuery(id+"F5.wireOp",EDGE,"E3.sketch_text.stroke-47"),sQuery(id+"F5.wireOp",EDGE,"E3.sketch_text.stroke-48"),sQuery(id+"F5.wireOp",EDGE,"E3.sketch_text.stroke-49"),sQuery(id+"F5.wireOp",EDGE,"E3.sketch_text.stroke-50"),sQuery(id+"F5.wireOp",EDGE,"E3.sketch_text.stroke-51"),sQuery(id+"F5.wireOp",EDGE,"E3.sketch_text.stroke-52"),sQuery(id+"F5.wireOp",EDGE,"E3.sketch_text.stroke-53"),sQuery(id+"F5.wireOp",EDGE,"E3.sketch_text.stroke-54"),sQuery(id+"F5.wireOp",EDGE,"E3.sketch_text.stroke-55"),sQuery(id+"F5.wireOp",EDGE,"E3.sketch_text.stroke-56"),sQuery(id+"F5.wireOp",EDGE,"E3.sketch_text.stroke-57"),sQuery(id+"F5.wireOp",EDGE,"E3.sketch_text.stroke-58")])],"isStart":false}),makeQuery(id+"F8.opExtrude","CAP_FACE",FACE,{"disambiguationData":[OSD([sQuery(id+"F5.wireOp",EDGE,"E3.sketch_text.stroke-59"),sQuery(id+"F5.wireOp",EDGE,"E3.sketch_text.stroke-60"),sQuery(id+"F5.wireOp",EDGE,"E3.sketch_text.stroke-61"),sQuery(id+"F5.wireOp",EDGE,"E3.sketch_text.stroke-62"),sQuery(id+"F5.wireOp",EDGE,"E3.sketch_text.stroke-63"),sQuery(id+"F5.wireOp",EDGE,"E3.sketch_text.stroke-64"),sQuery(id+"F5.wireOp",EDGE,"E3.sketch_text.stroke-65"),sQuery(id+"F5.wireOp",EDGE,"E3.sketch_text.stroke-66"),sQuery(id+"F5.wireOp",EDGE,"E3.sketch_text.stroke-67"),sQuery(id+"F5.wireOp",EDGE,"E3.sketch_text.stroke-68"),sQuery(id+"F5.wireOp",EDGE,"E3.sketch_text.stroke-69"),sQuery(id+"F5.wireOp",EDGE,"E3.sketch_text.stroke-70"),sQuery(id+"F5.wireOp",EDGE,"E3.sketch_text.stroke-71"),sQuery(id+"F5.wireOp",EDGE,"E3.sketch_text.stroke-72"),sQuery(id+"F5.wireOp",EDGE,"E3.sketch_text.stroke-73"),sQuery(id+"F5.wireOp",EDGE,"E3.sketch_text.stroke-74"),sQuery(id+"F5.wireOp",EDGE,"E3.sketch_text.stroke-75"),sQuery(id+"F5.wireOp",EDGE,"E3.sketch_text.stroke-76"),sQuery(id+"F5.wireOp",EDGE,"E3.sketch_text.stroke-77"),sQuery(id+"F5.wireOp",EDGE,"E3.sketch_text.stroke-78"),sQuery(id+"F5.wireOp",EDGE,"E3.sketch_text.stroke-79"),sQuery(id+"F5.wireOp",EDGE,"E3.sketch_text.stroke-80"),sQuery(id+"F5.wireOp",EDGE,"E3.sketch_text.stroke-81"),sQuery(id+"F5.wireOp",EDGE,"E3.sketch_text.stroke-82"),sQuery(id+"F5.wireOp",EDGE,"E3.sketch_text.stroke-83")])],"isStart":false}),makeQuery(id+"F8.opExtrude","CAP_FACE",FACE,{"disambiguationData":[OSD([sQuery(id+"F5.wireOp",EDGE,"E3.sketch_text.stroke-84"),sQuery(id+"F5.wireOp",EDGE,"E3.sketch_text.stroke-85"),sQuery(id+"F5.wireOp",EDGE,"E3.sketch_text.stroke-86"),sQuery(id+"F5.wireOp",EDGE,"E3.sketch_text.stroke-87"),sQuery(id+"F5.wireOp",EDGE,"E3.sketch_text.stroke-88"),sQuery(id+"F5.wireOp",EDGE,"E3.sketch_text.stroke-89"),sQuery(id+"F5.wireOp",EDGE,"E3.sketch_text.stroke-90"),sQuery(id+"F5.wireOp",EDGE,"E3.sketch_text.stroke-91"),sQuery(id+"F5.wireOp",EDGE,"E3.sketch_text.stroke-92"),sQuery(id+"F5.wireOp",EDGE,"E3.sketch_text.stroke-93"),sQuery(id+"F5.wireOp",EDGE,"E3.sketch_text.stroke-94"),sQuery(id+"F5.wireOp",EDGE,"E3.sketch_text.stroke-95"),sQuery(id+"F5.wireOp",EDGE,"E3.sketch_text.stroke-96"),sQuery(id+"F5.wireOp",EDGE,"E3.sketch_text.stroke-97")])],"isStart":false}),makeQuery(id+"F14.opExtrude","CAP_FACE",FACE,{"disambiguationData":[OSD([sQuery(id+"F11.wireOp",EDGE,"E10.bottom"),sQuery(id+"F11.wireOp",EDGE,"E10.top"),sQuery(id+"F11.wireOp",EDGE,"E10.left"),sQuery(id+"F11.wireOp",EDGE,"E10.right")])],"isStart":true}),makeQuery(id+"F14.opExtrude","CAP_FACE",FACE,{"disambiguationData":[OSD([sQuery(id+"F11.wireOp",EDGE,"E11.bottom"),sQuery(id+"F11.wireOp",EDGE,"E11.top"),sQuery(id+"F11.wireOp",EDGE,"E11.left"),sQuery(id+"F11.wireOp",EDGE,"E11.right")])],"isStart":true}),makeQuery(id+"F14.opExtrude","CAP_FACE",FACE,{"disambiguationData":[OSD([sQuery(id+"F11.wireOp",EDGE,"E12.bottom"),sQuery(id+"F11.wireOp",EDGE,"E12.top"),sQuery(id+"F11.wireOp",EDGE,"E12.left"),sQuery(id+"F11.wireOp",EDGE,"E12.right")])],"isStart":true}),makeQuery(id+"F14.opExtrude","CAP_FACE",FACE,{"disambiguationData":[OSD([sQuery(id+"F11.wireOp",EDGE,"E13.bottom"),sQuery(id+"F11.wireOp",EDGE,"E13.top"),sQuery(id+"F11.wireOp",EDGE,"E13.left"),sQuery(id+"F11.wireOp",EDGE,"E13.right")])],"isStart":true}),makeQuery(id+"F14.opExtrude","CAP_FACE",FACE,{"disambiguationData":[OSD([sQuery(id+"F11.wireOp",EDGE,"E14.bottom"),sQuery(id+"F11.wireOp",EDGE,"E14.top"),sQuery(id+"F11.wireOp",EDGE,"E14.left"),sQuery(id+"F11.wireOp",EDGE,"E14.right")])],"isStart":true})]});
            var sketch = newSketch(context, id + "F16", { "sketchPlane" : qUnion([Q0])});
            skLineSegment(sketch, "E15.0", {"start": v(-20, 17) * mm, "end": v(-20, 3.59) * mm});
            skLineSegment(sketch, "E15.1", {"start": v(20, 17) * mm, "end": v(20, -3.05) * mm});
            skLineSegment(sketch, "E16", {"start": v(-20, 4.77) * mm, "end": v(-20, -9.86) * mm});
            skLineSegment(sketch, "E17", {"start": v(20, -1.52) * mm, "end": v(20, -6.86) * mm});
            skSolve(sketch);
        }
        {
            var Q0;
            {var subQ0=makeQuery(id+"F8.opExtrude","CAP_EDGE",EDGE,{"disambiguationData":[OSD([sQuery(id+"F5.wireOp",EDGE,"E3.sketch_text.stroke-3")])],"isStart":false});Q0=makeQuery(id+"F16.imprint","IMPRINT",FACE,{"disambiguationData":[TD([[makeQuery(id+"F16.imprint","IMPRINT",EDGE,{"derivedFrom":subQ0}),1.0]])]});}
            var Q1;
            {var subQ0=makeQuery(id+"F8.opExtrude","CAP_EDGE",EDGE,{"disambiguationData":[OSD([sQuery(id+"F5.wireOp",EDGE,"E3.sketch_text.stroke-12")])],"isStart":false});Q1=makeQuery(id+"F16.imprint","IMPRINT",FACE,{"disambiguationData":[TD([[makeQuery(id+"F16.imprint","IMPRINT",EDGE,{"derivedFrom":subQ0}),1.0]])]});}
            var Q2;
            {var subQ5=makeQuery(id+"F8.opExtrude","CAP_EDGE",EDGE,{"disambiguationData":[OSD([sQuery(id+"F5.wireOp",EDGE,"E3.sketch_text.stroke-103")])],"isStart":false});Q2=makeQuery(id+"F16.imprint","IMPRINT",FACE,{"disambiguationData":[TD([[makeQuery(id+"F16.imprint","IMPRINT",EDGE,{"derivedFrom":subQ5}),1.0]])]});}
            extrude(context, id + "F17", {"entities" : qUnion([Q0, Q1, Q2]), "operationType" : NewBodyOperationType.REMOVE, "oppositeDirection" : true, "depth" : 2 * mm});
        }
    });
